# Revit family: Wall Mounted Lavatory Faucet(Short Spout)_TOTO_TLP02309
name_source: partatom
category: 衛生器具
revit_build: Autodesk Revit 2018 (Build: 20170223_1515(x64)
units: mm (PartAtom-declared; Revit-internal decimal feet)

## family parameters
OmniClass タイトル = Sanitary, Laundry, and Cleaning Equipment
OmniClass 番号 = 23.45.00.00
パーツ タイプ = 標準
ロード時にボイドで切り取り = いいえ
丸型コネクタ寸法 = 直径を使用
作業面ベース = いいえ
共有 = いいえ
常に垂直 = はい
部屋計算ポイント = いいえ

## types (1)
- Wall Mounted Lavatory Faucet(Short Spout)_TOTO_TLP02309
    Finish = faucet_material
    Height = 105.1
    Length = 203
    TOTO AsiaOceania = TLP02309B
    TOTO AsiaOceania URL = http://asia.toto.com
    TOTO China = TLP02309B1
    TOTO China URL = http://www.toto.com.cn
    TOTO Europe = TLP02309E
    TOTO Europe URL = https://gb.toto.com
    TOTO India = TLP02309B
    TOTO India URL = https://in.toto.com
    TOTO Korea = TLP02309KZL
    TOTO Korea URL = https://kr.toto.com
    TOTO Taiwan = TLP02309B
    TOTO Taiwan URL = https://www.twtoto.com.tw
    Width = 170
    タイプの説明 = without waste fitting/不含排水配件
    モデル = TLP02309
    製造元 = TOTO Ltd.
    説明 = Wall Mounted Lavatory Faucet(Short Spout)/单柄双控暗装洗面器水嘴(短款)

## geometry (parser evidence)
native form markers: Sweep x2
no freeform markers — native parametric forms only
